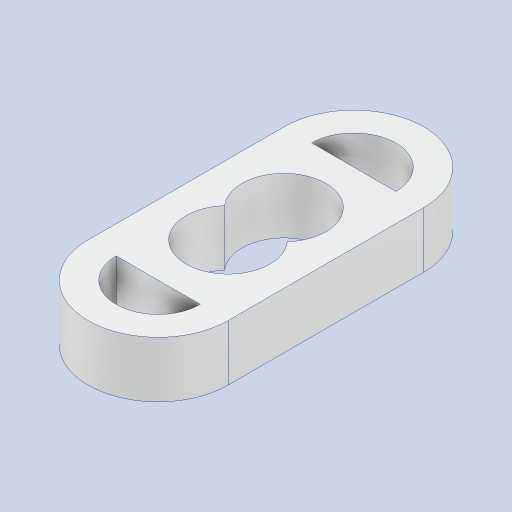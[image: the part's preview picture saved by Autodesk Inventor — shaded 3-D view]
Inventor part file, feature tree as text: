
AUTODESK INVENTOR PART (.ipt)
format: ipt  version: 2024 (Build 280153000, 153)  size: 245,248 bytes
history: native  units: mm
features: extrude x1, sketch x1
ambient origin geometry x8: Origin, YZ Plane, XZ Plane, XY Plane, X Axis, Y Axis, Z Axis, Center Point
bodies: Body1 (feature_tree)
feature tree (2):
  extrude  "Extrusión6"  Depth=20.0mm
  sketch  "Boceto1"  dims[d3=10.0mm d6=0.0mm d22=30.0mm d23=30.0mm d24=20.0mm d25=10.0mm d26=20.0mm d27=0.0mm d16=1.0mm d17=1.0mm d18=1.0mm d19=0.15mm d20=0.25mm d21=0.375mm]
